annotation { "Feature Type Name" : "Feature", "Feature Type Description" : "" }
export const myFeature = defineFeature(function(context is Context, id is Id, definition is map)
    precondition{}
    {
        {
            var Q0;
            Q0=qCreatedBy(makeId("Top.planeOp"),FACE);
            var sketch = newSketch(context, id + "F0", { "sketchPlane" : qUnion([Q0])});
            skLineSegment(sketch, "E0.bottom", {"start": v(-112.3, -4.07) * mm, "end": v(90.9, -4.07) * mm});
            skLineSegment(sketch, "E0.top", {"start": v(-112.3, -67.57) * mm, "end": v(90.9, -67.57) * mm});
            skLineSegment(sketch, "E0.left", {"start": v(-112.3, -4.07) * mm, "end": v(-112.3, -67.57) * mm});
            skLineSegment(sketch, "E0.right", {"start": v(90.9, -4.07) * mm, "end": v(90.9, -67.57) * mm});
            skSolve(sketch);
        }
        {
            var Q0;
            Q0 = qSketchRegion(id + "F0", true);
            extrude(context, id + "F1", {"entities" : qUnion([Q0]), "depth" : 6.35 * mm});
        }
        {
            var Q0;
            Q0=makeQuery(id+"F1.opExtrude","CAP_FACE",FACE,{"disambiguationData":[OSD([sQuery(id+"F0.wireOp",EDGE,"E0.bottom"),sQuery(id+"F0.wireOp",EDGE,"E0.top"),sQuery(id+"F0.wireOp",EDGE,"E0.left"),sQuery(id+"F0.wireOp",EDGE,"E0.right")])],"isStart":false});
            var sketch = newSketch(context, id + "F2", { "sketchPlane" : qUnion([Q0])});
            skLineSegment(sketch, "E1.bottom", {"start": v(-112.3, -32.77) * mm, "end": v(90.9, -32.77) * mm});
            skLineSegment(sketch, "E1.top", {"start": v(-112.3, -67.57) * mm, "end": v(90.9, -67.57) * mm});
            skLineSegment(sketch, "E1.left", {"start": v(-112.3, -32.77) * mm, "end": v(-112.3, -67.57) * mm});
            skLineSegment(sketch, "E1.right", {"start": v(90.9, -32.77) * mm, "end": v(90.9, -67.57) * mm});
            skLineSegment(sketch, "E2.bottom", {"start": v(-112.3, -4.07) * mm, "end": v(90.9, -4.07) * mm});
            skLineSegment(sketch, "E2.top", {"start": v(-112.3, -29.47) * mm, "end": v(90.9, -29.47) * mm});
            skLineSegment(sketch, "E2.left", {"start": v(-112.3, -4.07) * mm, "end": v(-112.3, -29.47) * mm});
            skLineSegment(sketch, "E2.right", {"start": v(90.9, -4.07) * mm, "end": v(90.9, -29.47) * mm});
            skSolve(sketch);
        }
        {
            var Q0;
            Q0 = qSketchRegion(id + "F2", true);
            extrude(context, id + "F3", {"entities" : qUnion([Q0]), "operationType" : NewBodyOperationType.ADD, "depth" : 6.35 * mm});
        }
        {
            var Q0;
            Q0=makeQuery(id+"F1.opExtrude","CAP_FACE",FACE,{"disambiguationData":[OSD([sQuery(id+"F0.wireOp",EDGE,"E0.bottom"),sQuery(id+"F0.wireOp",EDGE,"E0.top"),sQuery(id+"F0.wireOp",EDGE,"E0.left"),sQuery(id+"F0.wireOp",EDGE,"E0.right")])],"isStart":false});
            var sketch = newSketch(context, id + "F4", { "sketchPlane" : qUnion([Q0])});
            skLineSegment(sketch, "E3.bottom", {"start": v(90.9, -29.53) * mm, "end": v(-112.3, -29.53) * mm});
            skLineSegment(sketch, "E3.top", {"start": v(90.9, -32.7) * mm, "end": v(-112.3, -32.7) * mm});
            skLineSegment(sketch, "E3.left", {"start": v(90.9, -29.53) * mm, "end": v(90.9, -32.7) * mm});
            skLineSegment(sketch, "E3.right", {"start": v(-112.3, -29.53) * mm, "end": v(-112.3, -32.7) * mm});
            skSolve(sketch);
        }
        {
            var Q0;
            Q0 = qSketchRegion(id + "F4", true);
            extrude(context, id + "F5", {"entities" : qUnion([Q0]), "depth" : 45.72 * mm});
        }
        {
            var Q0;
            Q0=makeQuery(id+"F5.opExtrude","SWEPT_FACE",FACE,{"disambiguationData":[OSD([sQuery(id+"F4.wireOp",EDGE,"E3.top")])]});
            var sketch = newSketch(context, id + "F6", { "sketchPlane" : qUnion([Q0])});
            skCircle(sketch, "E4", {"center": v(-93.25, 33.02) * mm, "radius": 15.88 * mm});
            skText(sketch, "E5", { "text": "Cody Bindner\n", "fontName": "RobotoSlab-Regular.ttf"});
            skText(sketch, "E6", { "text": "Technical Co-op", "fontName": "RobotoSlab-Regular.ttf"});
            const initialGuessF6  = {"E5": [-0.06785, 0.04305, 1, 0, 0.0141], "E6": [-0.06785, 0.03093, 1, 0, 0.0059]};
            skSetInitialGuess(sketch, initialGuessF6);
            skSolve(sketch);
        }
        {
            var Q0;
            Q0 = qSketchRegion(id + "F6", true);
            extrude(context, id + "F7", {"entities" : qUnion([Q0]), "operationType" : NewBodyOperationType.REMOVE, "oppositeDirection" : true, "depth" : 2.54 * mm});
        }
    });